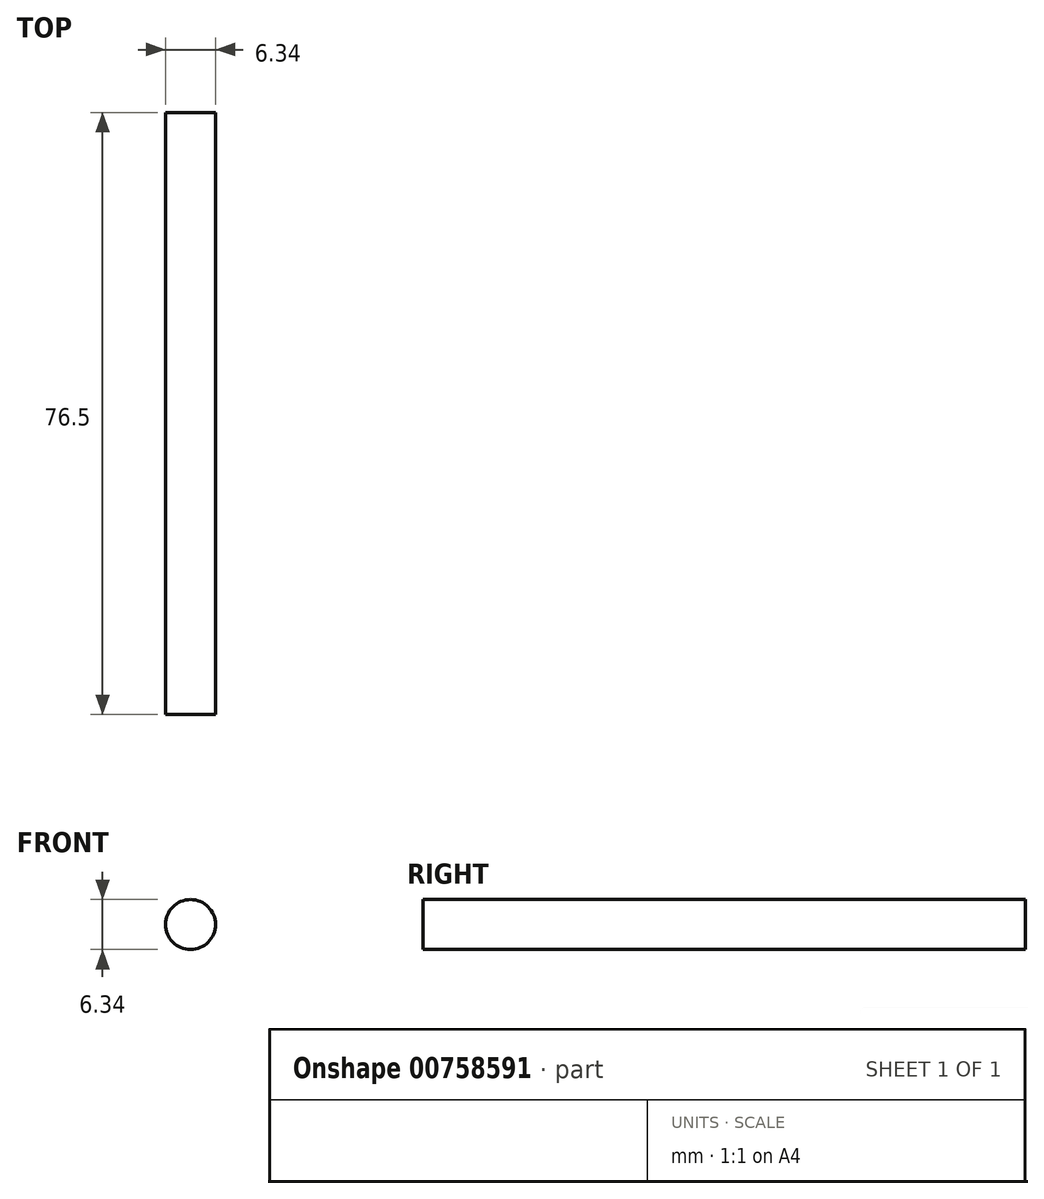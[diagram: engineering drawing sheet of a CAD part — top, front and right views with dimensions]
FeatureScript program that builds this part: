
annotation { "Feature Type Name" : "Feature", "Feature Type Description" : "" }
export const myFeature = defineFeature(function(context is Context, id is Id, definition is map)
    precondition{}
    {
        {
            var Q0;
            Q0=qCreatedBy(makeId("Front.planeOp"),FACE);
            var sketch = newSketch(context, id + "F0", { "sketchPlane" : qUnion([Q0])});
            skCircle(sketch, "E0", {"center": v(0, 0) * mm, "radius": 3.17 * mm});
            skSolve(sketch);
        }
        {
            var Q0;
            Q0=makeQuery(id+"F0.imprint","IMPRINT",FACE,{"disambiguationData":[TD([[makeQuery(id+"F0.imprint","IMPRINT",EDGE,{"derivedFrom":sQuery(id+"F0.wireOp",EDGE,"E0")}),1.0]])]});
            extrude(context, id + "F1", {"entities" : qUnion([Q0]), "depth" : 76.5 * mm, "offsetDistance" : 25 * mm});
        }
    });
